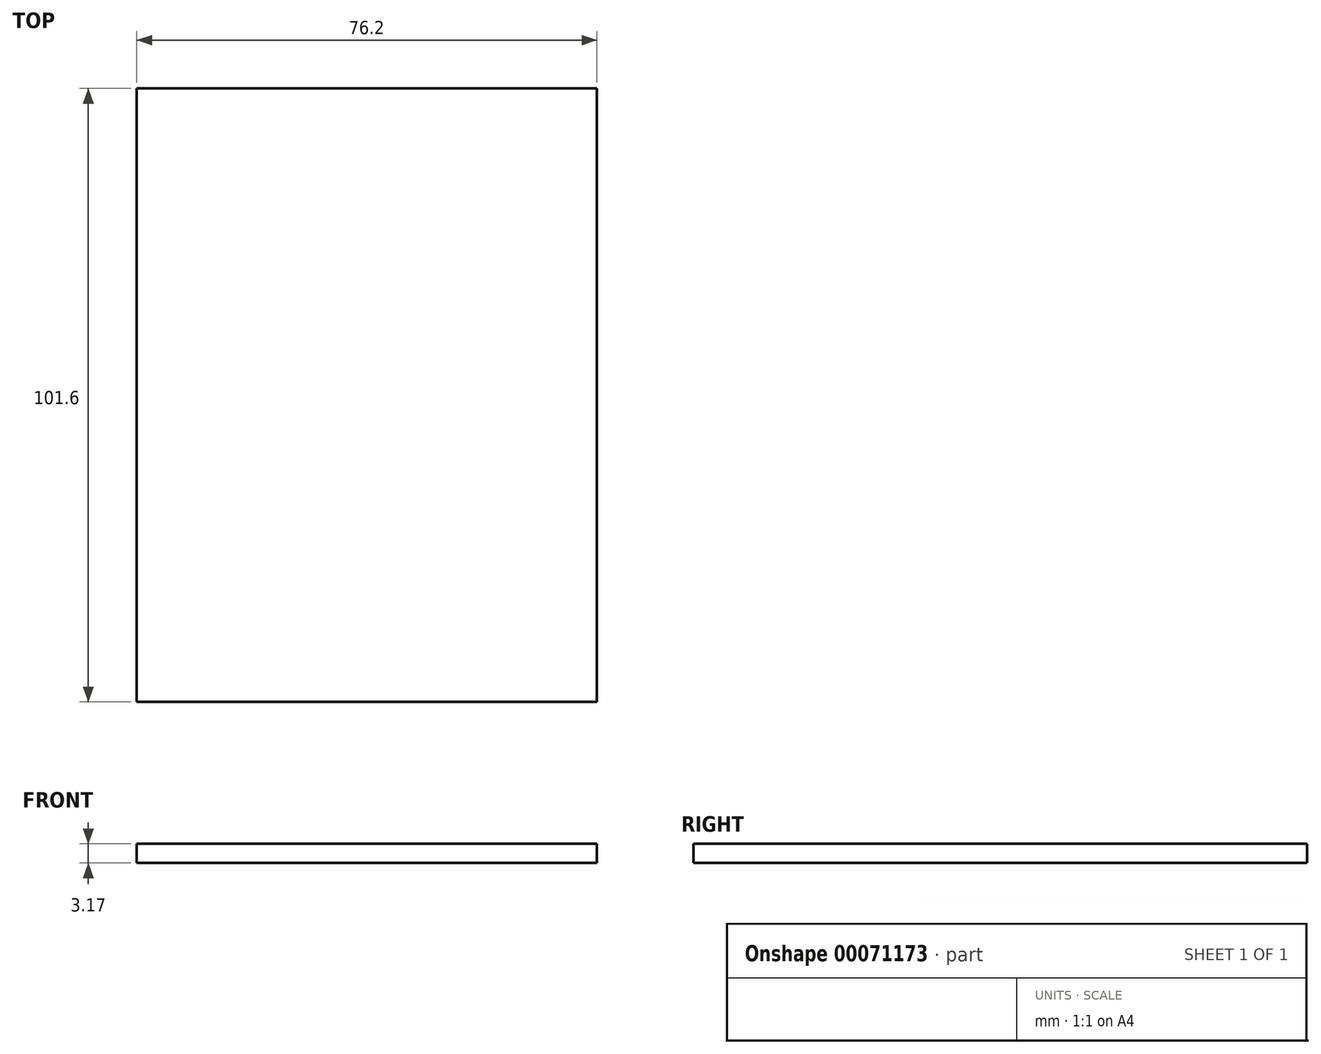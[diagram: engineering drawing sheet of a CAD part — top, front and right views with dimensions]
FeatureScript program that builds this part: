
annotation { "Feature Type Name" : "Feature", "Feature Type Description" : "" }
export const myFeature = defineFeature(function(context is Context, id is Id, definition is map)
    precondition{}
    {
        {
            var Q0;
            Q0=qCreatedBy(makeId("Top.planeOp"),FACE);
            var sketch = newSketch(context, id + "F0", { "sketchPlane" : qUnion([Q0])});
            skLineSegment(sketch, "E0.rect.bottom", {"start": v(38.1, 50.8) * mm, "end": v(-38.1, 50.8) * mm});
            skLineSegment(sketch, "E0.rect.top", {"start": v(38.1, -50.8) * mm, "end": v(-38.1, -50.8) * mm});
            skLineSegment(sketch, "E0.rect.left", {"start": v(38.1, 50.8) * mm, "end": v(38.1, -50.8) * mm});
            skLineSegment(sketch, "E0.rect.right", {"start": v(-38.1, 50.8) * mm, "end": v(-38.1, -50.8) * mm});
            skPoint(sketch, "E0.rect.middle", {"position": v(0, 0) * mm});
            skSolve(sketch);
        }
        {
            var Q0;
            Q0=makeQuery(id+"F0.imprint","IMPRINT",FACE,{"disambiguationData":[TD([[makeQuery(id+"F0.imprint","IMPRINT",EDGE,{"derivedFrom":sQuery(id+"F0.wireOp",EDGE,"E0.rect.bottom")}),1.0]])]});
            extrude(context, id + "F1", {"entities" : qUnion([Q0]), "depth" : 3.17 * mm});
        }
    });
